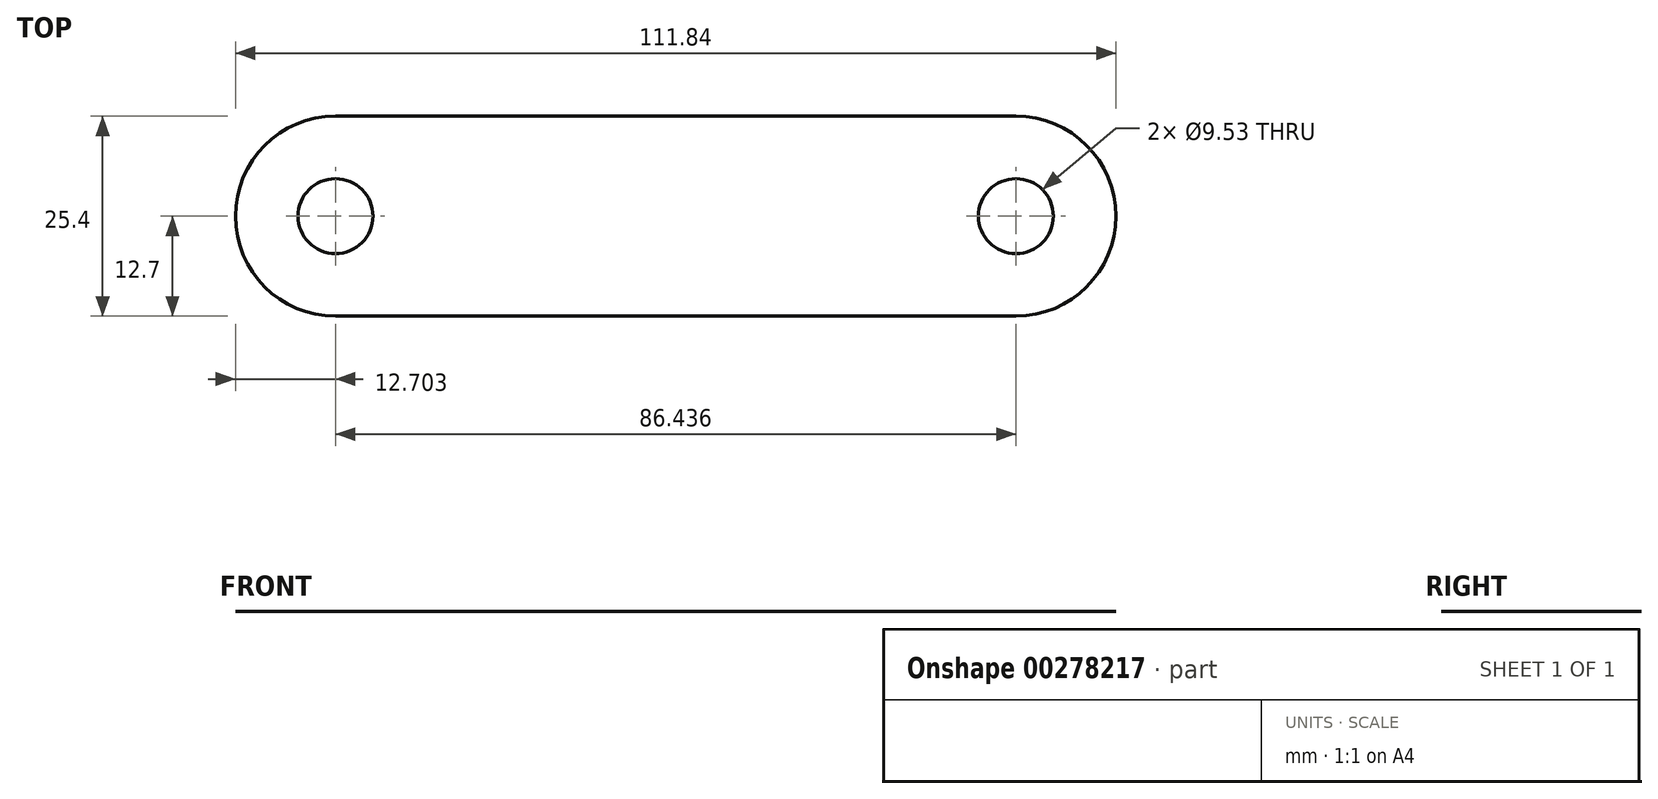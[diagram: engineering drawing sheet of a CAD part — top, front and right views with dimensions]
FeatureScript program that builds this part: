
annotation { "Feature Type Name" : "Feature", "Feature Type Description" : "" }
export const myFeature = defineFeature(function(context is Context, id is Id, definition is map)
    precondition{}
    {
        {
            var Q0;
            Q0=qCreatedBy(makeId("Top.planeOp"),FACE);
            var sketch = newSketch(context, id + "F0", { "sketchPlane" : qUnion([Q0])});
            skLineSegment(sketch, "E0", {"start": v(-41.5, 0) * mm, "end": v(44.94, 0) * mm});
            skCircle(sketch, "E1", {"center": v(-41.5, 0) * mm, "radius": 12.7 * mm});
            skCircle(sketch, "E2", {"center": v(44.94, 0) * mm, "radius": 12.7 * mm});
            skCircle(sketch, "E3", {"center": v(-41.5, 0) * mm, "radius": 4.76 * mm});
            skCircle(sketch, "E4", {"center": v(44.94, 0) * mm, "radius": 4.76 * mm});
            skLineSegment(sketch, "E5", {"start": v(-41.5, 12.7) * mm, "end": v(44.94, 12.7) * mm});
            skLineSegment(sketch, "E6", {"start": v(-41.5, 0) * mm, "end": v(-41.5, -12.7) * mm});
            skLineSegment(sketch, "E7", {"start": v(-41.5, -12.7) * mm, "end": v(44.94, -12.7) * mm});
            skSolve(sketch);
        }
        {
            var Q0;
            {var subQ5=sQuery(id+"F0.wireOp",EDGE,"E5");Q0=makeQuery(id+"F0.imprint","IMPRINT",FACE,{"disambiguationData":[TD([[makeQuery(id+"F0.imprint","IMPRINT",EDGE,{"derivedFrom":subQ5}),-1.0]])]});}
            var Q1;
            {var subQ0=sQuery(id+"F0.wireOp",EDGE,"E3");var subQ1=sQuery(id+"F0.wireOp",EDGE,"E0");var subQ2=makeQuery(id+"F0.imprint","INTERSECT",VERTEX,{"derivedFrom":[subQ1,subQ0]});Q1=makeQuery(id+"F0.imprint","IMPRINT",FACE,{"disambiguationData":[TD([[makeQuery(id+"F0.imprint","IMPRINT",EDGE,{"disambiguationData":[TD([[subQ2,-1.0]])],"derivedFrom":subQ1}),1.0]])]});}
            var Q2;
            {var subQ0=sQuery(id+"F0.wireOp",EDGE,"E3");var subQ1=sQuery(id+"F0.wireOp",EDGE,"E0");var subQ2=makeQuery(id+"F0.imprint","INTERSECT",VERTEX,{"derivedFrom":[subQ1,subQ0]});Q2=makeQuery(id+"F0.imprint","IMPRINT",FACE,{"disambiguationData":[TD([[makeQuery(id+"F0.imprint","IMPRINT",EDGE,{"disambiguationData":[TD([[subQ2,-1.0]])],"derivedFrom":subQ1}),-1.0]])]});}
            var Q3;
            {var subQ5=sQuery(id+"F0.wireOp",EDGE,"E7");Q3=makeQuery(id+"F0.imprint","IMPRINT",FACE,{"disambiguationData":[TD([[makeQuery(id+"F0.imprint","IMPRINT",EDGE,{"derivedFrom":subQ5}),1.0]])]});}
            var Q4;
            Q4=makeQuery(id+"F0.imprint","IMPRINT",FACE,{"disambiguationData":[TD([[makeQuery(id+"F0.imprint","IMPRINT",EDGE,{"derivedFrom":sQuery(id+"F0.wireOp",EDGE,"E4")}),-1.0]])]});
            extrude(context, id + "F1", {"entities" : qUnion([Q0, Q1, Q2, Q3, Q4]), "depth" : 1 / 203.2 * mm});
        }
    });
